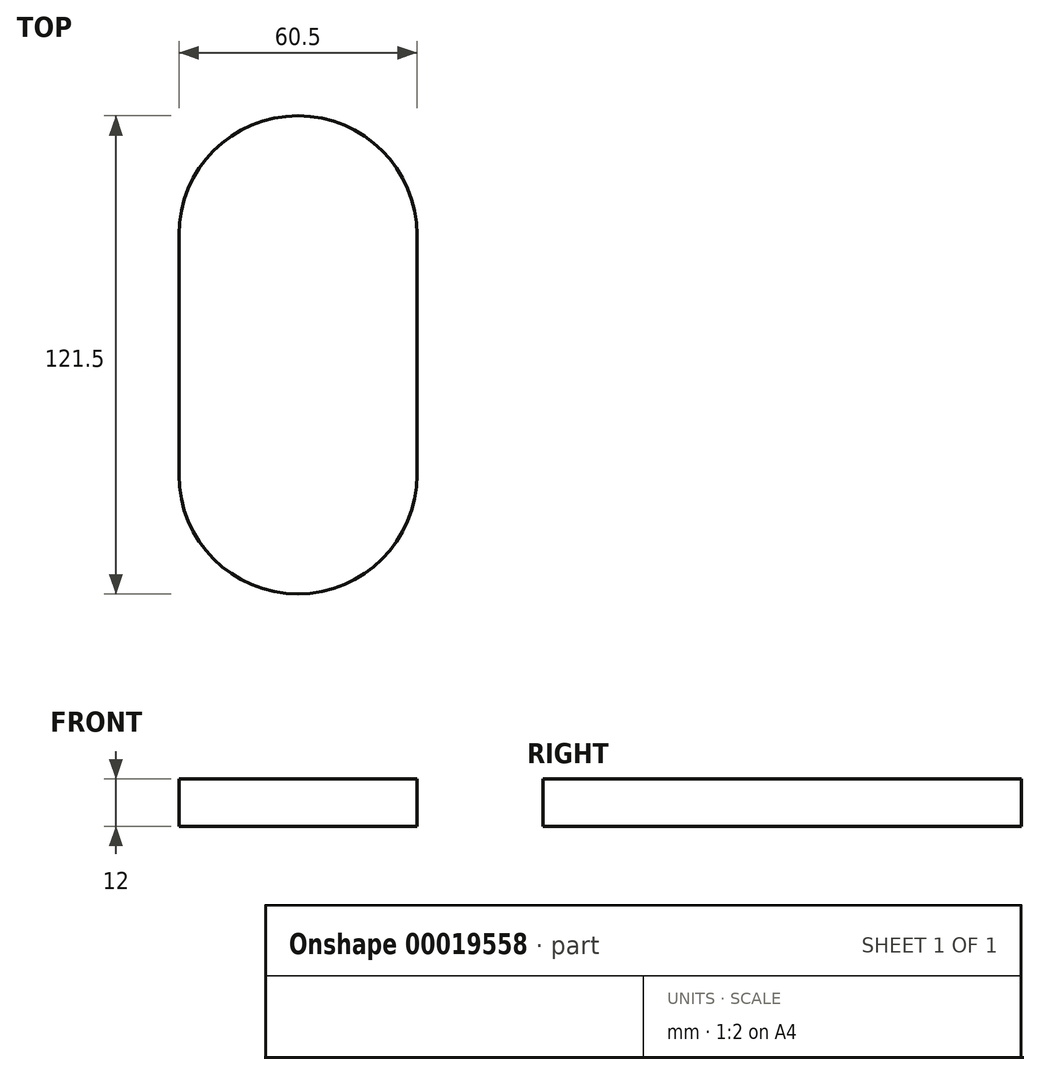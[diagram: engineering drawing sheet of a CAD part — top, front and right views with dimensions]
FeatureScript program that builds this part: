
annotation { "Feature Type Name" : "Feature", "Feature Type Description" : "" }
export const myFeature = defineFeature(function(context is Context, id is Id, definition is map)
    precondition{}
    {
        {
            var Q0;
            Q0=qCreatedBy(makeId("Top.planeOp"),FACE);
            var sketch = newSketch(context, id + "F0", { "sketchPlane" : qUnion([Q0])});
            skArc(sketch, "E0", {"start": v(30.25, 0) * mm, "mid": v(0, 30.25) * mm, "end": v(-30.25, 0) * mm});
            skArc(sketch, "E1", {"start": v(-30.25, -61) * mm, "mid": v(0, -91.25) * mm, "end": v(30.25, -61) * mm});
            skLineSegment(sketch, "E2", {"start": v(-30.25, 0) * mm, "end": v(-30.25, -61) * mm});
            skLineSegment(sketch, "E3", {"start": v(30.25, 0) * mm, "end": v(30.25, -61) * mm});
            skSolve(sketch);
        }
        {
            var Q0;
            Q0 = qSketchRegion(id + "F0", true);
            extrude(context, id + "F1", {"entities" : qUnion([Q0]), "depth" : 12 * mm});
        }
    });
